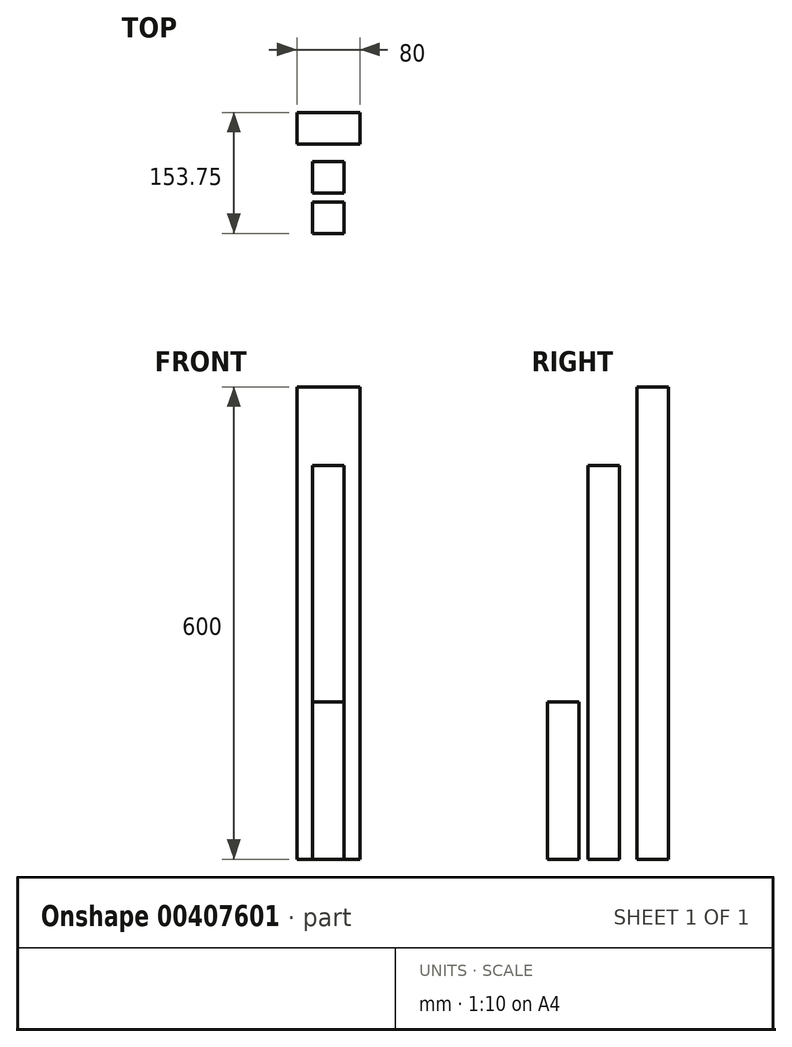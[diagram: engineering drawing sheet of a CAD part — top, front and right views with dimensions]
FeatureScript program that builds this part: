
annotation { "Feature Type Name" : "Feature", "Feature Type Description" : "" }
export const myFeature = defineFeature(function(context is Context, id is Id, definition is map)
    precondition{}
    {
        {
            assignVariable(context, id + "F0", {"name" : "ye", "anyValue" : 600});
        }
        {
            assignVariable(context, id + "F1", {"name" : "xe", "anyValue" : 500});
        }
        {
            assignVariable(context, id + "F2", {"name" : "ze", "anyValue" : 200});
        }
        {
            var Q0;
            Q0=qCreatedBy(makeId("Top.planeOp"),FACE);
            var sketch = newSketch(context, id + "F3", { "sketchPlane" : qUnion([Q0])});
            skLineSegment(sketch, "E0.bottom", {"start": v(40, 20) * mm, "end": v(-40, 20) * mm});
            skLineSegment(sketch, "E0.top", {"start": v(40, -20) * mm, "end": v(-40, -20) * mm});
            skLineSegment(sketch, "E0.left", {"start": v(40, 20) * mm, "end": v(40, -20) * mm});
            skLineSegment(sketch, "E0.right", {"start": v(-40, 20) * mm, "end": v(-40, -20) * mm});
            skPoint(sketch, "E0.middle", {"position": v(0, 0) * mm});
            skLineSegment(sketch, "E1", {"start": v(0, 61.72) * mm, "end": v(0, -129.89) * mm, "construction": true});
            skLineSegment(sketch, "E2.bottom", {"start": v(20, -82.5) * mm, "end": v(-20, -82.5) * mm});
            skLineSegment(sketch, "E2.top", {"start": v(20, -42.5) * mm, "end": v(-20, -42.5) * mm});
            skLineSegment(sketch, "E2.left", {"start": v(20, -82.5) * mm, "end": v(20, -42.5) * mm});
            skLineSegment(sketch, "E2.right", {"start": v(-20, -82.5) * mm, "end": v(-20, -42.5) * mm});
            skPoint(sketch, "E2.middle", {"position": v(0, -62.5) * mm});
            skLineSegment(sketch, "E3.bottom", {"start": v(20, -133.75) * mm, "end": v(-20, -133.75) * mm});
            skLineSegment(sketch, "E3.top", {"start": v(20, -93.75) * mm, "end": v(-20, -93.75) * mm});
            skLineSegment(sketch, "E3.left", {"start": v(20, -133.75) * mm, "end": v(20, -93.75) * mm});
            skLineSegment(sketch, "E3.right", {"start": v(-20, -133.75) * mm, "end": v(-20, -93.75) * mm});
            skPoint(sketch, "E3.middle", {"position": v(0, -113.75) * mm});
            skLineSegment(sketch, "E4.1.0.0", {"start": v(150, 20) * mm, "end": v(150, -20) * mm});
            skLineSegment(sketch, "E4.1.0.1", {"start": v(150, 20) * mm, "end": v(70, 20) * mm});
            skLineSegment(sketch, "E4.1.0.2", {"start": v(70, 20) * mm, "end": v(70, -20) * mm});
            skLineSegment(sketch, "E4.1.0.3", {"start": v(150, -20) * mm, "end": v(70, -20) * mm});
            skLineSegment(sketch, "E4.1.0.4", {"start": v(90, -82.5) * mm, "end": v(90, -42.5) * mm});
            skLineSegment(sketch, "E4.1.0.5", {"start": v(130, -42.5) * mm, "end": v(90, -42.5) * mm});
            skLineSegment(sketch, "E4.1.0.6", {"start": v(130, -82.5) * mm, "end": v(130, -42.5) * mm});
            skLineSegment(sketch, "E4.1.0.7", {"start": v(130, -82.5) * mm, "end": v(90, -82.5) * mm});
            skLineSegment(sketch, "E4.1.0.8", {"start": v(90, -133.75) * mm, "end": v(90, -93.75) * mm});
            skLineSegment(sketch, "E4.1.0.9", {"start": v(130, -93.75) * mm, "end": v(90, -93.75) * mm});
            skLineSegment(sketch, "E4.1.0.10", {"start": v(130, -133.75) * mm, "end": v(90, -133.75) * mm});
            skLineSegment(sketch, "E4.1.0.11", {"start": v(130, -133.75) * mm, "end": v(130, -93.75) * mm});
            skLineSegment(sketch, "E4.2.0.0", {"start": v(260, 20) * mm, "end": v(260, -20) * mm});
            skLineSegment(sketch, "E4.2.0.1", {"start": v(260, 20) * mm, "end": v(180, 20) * mm});
            skLineSegment(sketch, "E4.2.0.2", {"start": v(180, 20) * mm, "end": v(180, -20) * mm});
            skLineSegment(sketch, "E4.2.0.3", {"start": v(260, -20) * mm, "end": v(180, -20) * mm});
            skLineSegment(sketch, "E4.2.0.4", {"start": v(200, -82.5) * mm, "end": v(200, -42.5) * mm});
            skLineSegment(sketch, "E4.2.0.5", {"start": v(240, -42.5) * mm, "end": v(200, -42.5) * mm});
            skLineSegment(sketch, "E4.2.0.6", {"start": v(240, -82.5) * mm, "end": v(240, -42.5) * mm});
            skLineSegment(sketch, "E4.2.0.7", {"start": v(240, -82.5) * mm, "end": v(200, -82.5) * mm});
            skLineSegment(sketch, "E4.2.0.8", {"start": v(200, -133.75) * mm, "end": v(200, -93.75) * mm});
            skLineSegment(sketch, "E4.2.0.9", {"start": v(240, -93.75) * mm, "end": v(200, -93.75) * mm});
            skLineSegment(sketch, "E4.2.0.10", {"start": v(240, -133.75) * mm, "end": v(200, -133.75) * mm});
            skLineSegment(sketch, "E4.2.0.11", {"start": v(240, -133.75) * mm, "end": v(240, -93.75) * mm});
            skLineSegment(sketch, "E4.direction1", {"start": v(40, -20) * mm, "end": v(150, -20) * mm, "construction": true});
            skSolve(sketch);
        }
        {
            var Q0;
            Q0=makeQuery(id+"F3.imprint","IMPRINT",FACE,{"disambiguationData":[TD([[makeQuery(id+"F3.imprint","IMPRINT",EDGE,{"derivedFrom":sQuery(id+"F3.wireOp",EDGE,"E0.bottom")}),1.0]])]});
            extrude(context, id + "F4", {"entities" : qUnion([Q0]), "depth" : (getVariable(context, 'ye')) * mm});
        }
        {
            var Q0;
            Q0=makeQuery(id+"F3.imprint","IMPRINT",FACE,{"disambiguationData":[TD([[makeQuery(id+"F3.imprint","IMPRINT",EDGE,{"derivedFrom":sQuery(id+"F3.wireOp",EDGE,"E2.bottom")}),-1.0]])]});
            extrude(context, id + "F5", {"entities" : qUnion([Q0]), "depth" : (getVariable(context, 'xe')) * mm});
        }
        {
            var Q0;
            Q0=makeQuery(id+"F3.imprint","IMPRINT",FACE,{"disambiguationData":[TD([[makeQuery(id+"F3.imprint","IMPRINT",EDGE,{"derivedFrom":sQuery(id+"F3.wireOp",EDGE,"E3.bottom")}),-1.0]])]});
            extrude(context, id + "F6", {"entities" : qUnion([Q0]), "depth" : (getVariable(context, 'ze')) * mm});
        }
    });
